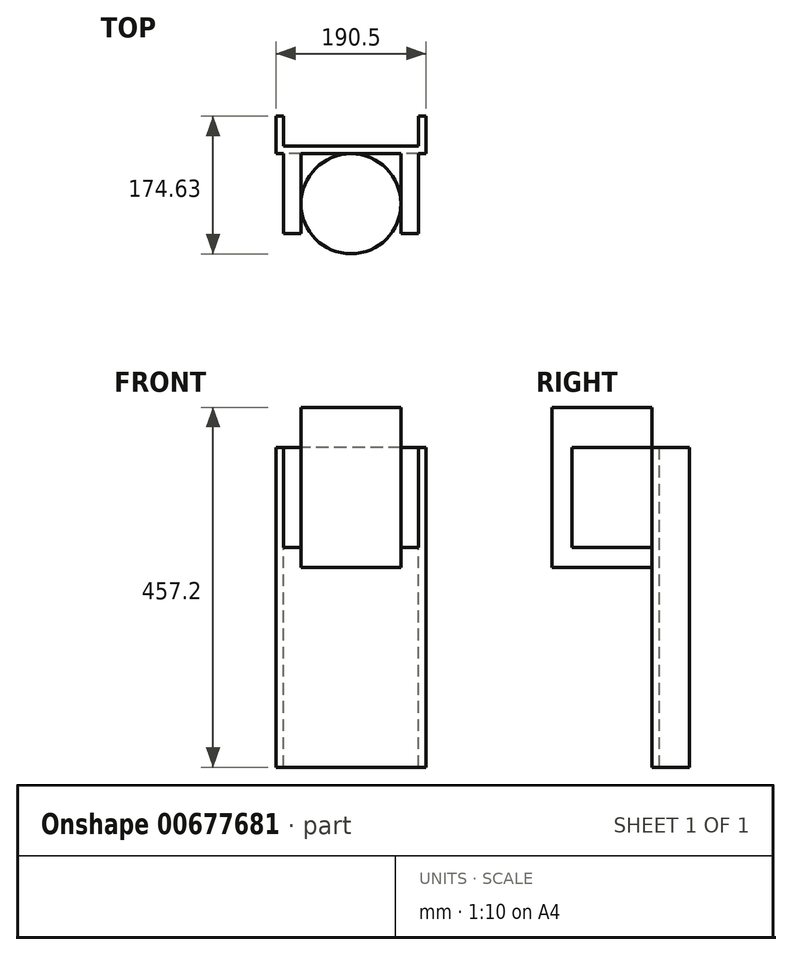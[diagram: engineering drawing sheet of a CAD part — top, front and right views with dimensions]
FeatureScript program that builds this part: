
annotation { "Feature Type Name" : "Feature", "Feature Type Description" : "" }
export const myFeature = defineFeature(function(context is Context, id is Id, definition is map)
    precondition{}
    {
        {
            var Q0;
            Q0=qCreatedBy(makeId("Front.planeOp"),FACE);
            var sketch = newSketch(context, id + "F0", { "sketchPlane" : qUnion([Q0])});
            skLineSegment(sketch, "E0.bottom", {"start": v(0, 0) * mm, "end": v(171.45, 0) * mm});
            skLineSegment(sketch, "E0.top", {"start": v(0, 406.4) * mm, "end": v(171.45, 406.4) * mm});
            skLineSegment(sketch, "E0.left", {"start": v(0, 0) * mm, "end": v(0, 406.4) * mm});
            skLineSegment(sketch, "E0.right", {"start": v(171.45, 0) * mm, "end": v(171.45, 406.4) * mm});
            skLineSegment(sketch, "E1.bottom", {"start": v(0, 406.4) * mm, "end": v(-9.53, 406.4) * mm});
            skLineSegment(sketch, "E1.top", {"start": v(0, 0) * mm, "end": v(-9.52, 0) * mm});
            skLineSegment(sketch, "E1.left", {"start": v(0, 406.4) * mm, "end": v(0, 0) * mm});
            skLineSegment(sketch, "E1.right", {"start": v(-9.53, 406.4) * mm, "end": v(-9.52, 0) * mm});
            skLineSegment(sketch, "E2.bottom", {"start": v(171.45, 406.4) * mm, "end": v(180.97, 406.4) * mm});
            skLineSegment(sketch, "E2.top", {"start": v(171.45, 0) * mm, "end": v(180.97, 0) * mm});
            skLineSegment(sketch, "E2.left", {"start": v(171.45, 406.4) * mm, "end": v(171.45, 0) * mm});
            skLineSegment(sketch, "E2.right", {"start": v(180.97, 406.4) * mm, "end": v(180.97, 0) * mm});
            skSolve(sketch);
        }
        {
            var Q0;
            Q0=makeQuery(id+"F0.imprint","IMPRINT",FACE,{"disambiguationData":[TD([[makeQuery(id+"F0.imprint","IMPRINT",EDGE,{"derivedFrom":sQuery(id+"F0.wireOp",EDGE,"E1.bottom")}),1.0]])]});
            var Q1;
            Q1=makeQuery(id+"F0.imprint","IMPRINT",FACE,{"disambiguationData":[TD([[makeQuery(id+"F0.imprint","IMPRINT",EDGE,{"derivedFrom":sQuery(id+"F0.wireOp",EDGE,"E0.bottom")}),1.0]])]});
            var Q2;
            Q2=makeQuery(id+"F0.imprint","IMPRINT",FACE,{"disambiguationData":[TD([[makeQuery(id+"F0.imprint","IMPRINT",EDGE,{"derivedFrom":sQuery(id+"F0.wireOp",EDGE,"E2.bottom")}),-1.0]])]});
            extrude(context, id + "F1", {"entities" : qUnion([Q0, Q1, Q2]), "depth" : 9.52 * mm, "offsetDistance" : 25.4 * mm});
        }
        {
            var Q0;
            Q0=makeQuery(id+"F0.imprint","IMPRINT",FACE,{"disambiguationData":[TD([[makeQuery(id+"F0.imprint","IMPRINT",EDGE,{"derivedFrom":sQuery(id+"F0.wireOp",EDGE,"E2.bottom")}),-1.0]])]});
            var Q1;
            Q1=makeQuery(id+"F0.imprint","IMPRINT",FACE,{"disambiguationData":[TD([[makeQuery(id+"F0.imprint","IMPRINT",EDGE,{"derivedFrom":sQuery(id+"F0.wireOp",EDGE,"E1.bottom")}),1.0]])]});
            extrude(context, id + "F2", {"entities" : qUnion([Q0, Q1]), "operationType" : NewBodyOperationType.ADD, "oppositeDirection" : true, "depth" : 38.1 * mm, "offsetDistance" : 25.4 * mm});
        }
        {
            var Q0;
            {var subQ0=sQuery(id+"F0.wireOp",EDGE,"E2.bottom");var subQ1=sQuery(id+"F0.wireOp",EDGE,"E1.bottom");Q0=makeQuery(id+"F2.boolean.opBoolean","MERGE",FACE,{"derivedFrom":[makeQuery(id+"F1.opExtrude","SWEPT_FACE",FACE,{"disambiguationData":[OSD([sQuery(id+"F0.wireOp",EDGE,"E0.top"),subQ1,subQ0])]}),makeQuery(id+"F2.opExtrude","SWEPT_FACE",FACE,{"disambiguationData":[OSD([subQ1])]}),makeQuery(id+"F2.opExtrude","SWEPT_FACE",FACE,{"disambiguationData":[OSD([subQ0])]})]});}
            var sketch = newSketch(context, id + "F3", { "sketchPlane" : qUnion([Q0])});
            skLineSegment(sketch, "E3", {"start": v(85.72, -9.53) * mm, "end": v(85.72, -154.44) * mm, "construction": true});
            skPoint(sketch, "E4", {"position": v(85.72, -73.03) * mm});
            skPoint(sketch, "E5", {"position": v(85.72, -9.53) * mm});
            skCircle(sketch, "E6", {"center": v(85.72, -73.03) * mm, "radius": 63.5 * mm});
            skLineSegment(sketch, "E7.left", {"start": v(22.22, -73.03) * mm, "end": v(22.22, -111.13) * mm});
            skLineSegment(sketch, "E7.right", {"start": v(149.73, -73.03) * mm, "end": v(149.73, -111.13) * mm});
            skLineSegment(sketch, "E8.bottom", {"start": v(22.22, -111.13) * mm, "end": v(0, -111.13) * mm});
            skLineSegment(sketch, "E8.top", {"start": v(22.22, -9.53) * mm, "end": v(0, -9.53) * mm});
            skLineSegment(sketch, "E8.left", {"start": v(22.22, -111.13) * mm, "end": v(22.22, -9.52) * mm});
            skLineSegment(sketch, "E8.right", {"start": v(0, -111.13) * mm, "end": v(0, -9.52) * mm});
            skLineSegment(sketch, "E9.MirrorCS", {"start": v(149.22, -111.13) * mm, "end": v(149.22, -9.52) * mm});
            skLineSegment(sketch, "E10.MirrorCS", {"start": v(149.22, -73.03) * mm, "end": v(149.22, -111.13) * mm});
            skLineSegment(sketch, "E11.MirrorCS", {"start": v(171.45, -111.13) * mm, "end": v(171.45, -9.52) * mm});
            skLineSegment(sketch, "E12.MirrorCS", {"start": v(149.22, -111.13) * mm, "end": v(171.45, -111.13) * mm});
            skLineSegment(sketch, "E13.trimOffspring", {"start": v(149.22, -111.13) * mm, "end": v(149.73, -111.13) * mm});
            skSolve(sketch);
        }
        {
            var Q0;
            {var subQ0=sQuery(id+"F3.wireOp",EDGE,"E6");var subQ3=makeQuery(id+"F3.imprint","INTERSECT",VERTEX,{"derivedFrom":[subQ0,sQuery(id+"F3.wireOp",EDGE,"E8.left")]});Q0=makeQuery(id+"F3.imprint","IMPRINT",FACE,{"disambiguationData":[TD([[makeQuery(id+"F3.imprint","IMPRINT",EDGE,{"disambiguationData":[TD([[subQ3,-1.0]])],"derivedFrom":subQ0}),1.0]])]});}
            extrude(context, id + "F4", {"entities" : qUnion([Q0]), "operationType" : NewBodyOperationType.ADD, "oppositeDirection" : true, "depth" : 152.4 * mm, "offsetDistance" : 25.4 * mm, "hasSecondDirection" : true, "secondDirectionOppositeDirection" : false, "secondDirectionDepth" : 50.8 * mm});
        }
        {
            var Q0;
            {var subQ0=sQuery(id+"F3.wireOp",EDGE,"E9.MirrorCS");Q0=makeQuery(id+"F3.imprint","IMPRINT",FACE,{"disambiguationData":[TD([[makeQuery(id+"F3.imprint","IMPRINT",EDGE,{"derivedFrom":subQ0}),-1.0]])]});}
            var Q1;
            {var subQ3=sQuery(id+"F3.wireOp",EDGE,"E8.bottom");Q1=makeQuery(id+"F3.imprint","IMPRINT",FACE,{"disambiguationData":[TD([[makeQuery(id+"F3.imprint","IMPRINT",EDGE,{"derivedFrom":subQ3}),-1.0]])]});}
            extrude(context, id + "F5", {"entities" : qUnion([Q0, Q1]), "operationType" : NewBodyOperationType.ADD, "oppositeDirection" : true, "depth" : 127 * mm, "offsetDistance" : 25.4 * mm});
        }
    });
